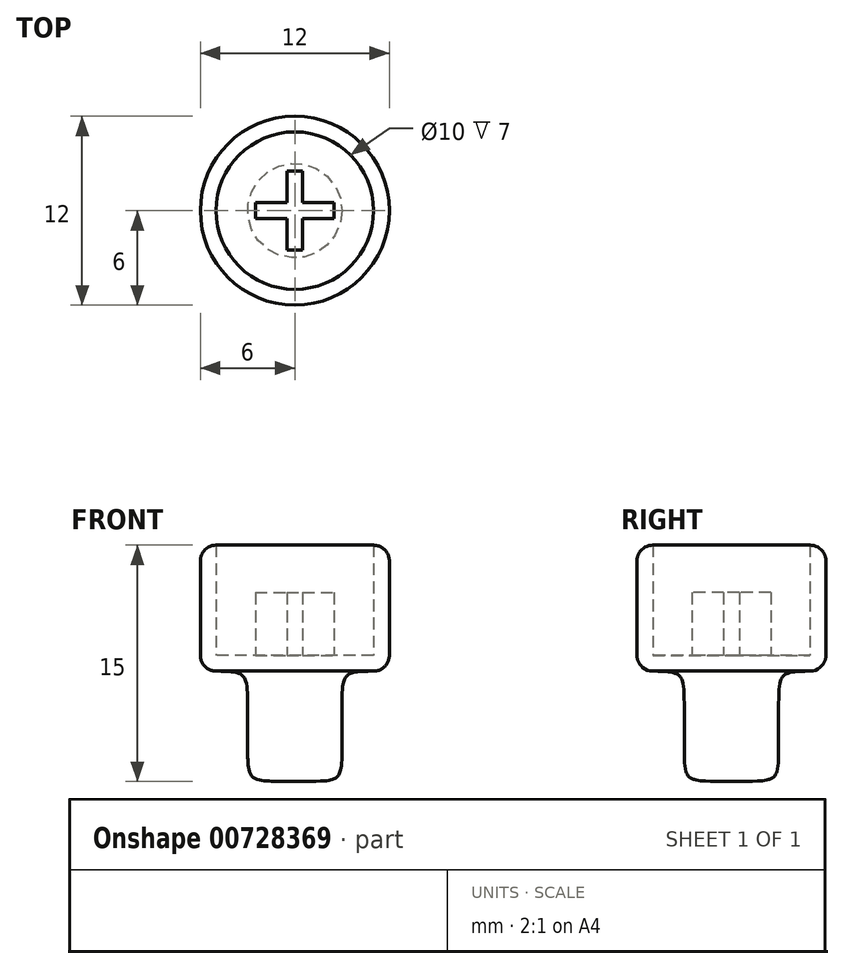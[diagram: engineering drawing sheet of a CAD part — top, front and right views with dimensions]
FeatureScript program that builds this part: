
annotation { "Feature Type Name" : "Feature", "Feature Type Description" : "" }
export const myFeature = defineFeature(function(context is Context, id is Id, definition is map)
    precondition{}
    {
        {
            var Q0;
            Q0=qCreatedBy(makeId("Top.planeOp"),FACE);
            var sketch = newSketch(context, id + "F0", { "sketchPlane" : qUnion([Q0])});
            skCircle(sketch, "E0", {"center": v(0, 0) * mm, "radius": 3 * mm});
            skSolve(sketch);
        }
        {
            var Q0;
            Q0=makeQuery(id+"F0.imprint","IMPRINT",FACE,{"disambiguationData":[TD([[makeQuery(id+"F0.imprint","IMPRINT",EDGE,{"derivedFrom":sQuery(id+"F0.wireOp",EDGE,"E0")}),1.0]])]});
            extrude(context, id + "F1", {"entities" : qUnion([Q0]), "depth" : 7 * mm, "offsetDistance" : 25 * mm});
        }
        {
            var Q0;
            Q0=makeQuery(id+"F1.opExtrude","CAP_FACE",FACE,{"disambiguationData":[OSD([sQuery(id+"F0.wireOp",EDGE,"E0")])],"isStart":false});
            var sketch = newSketch(context, id + "F2", { "sketchPlane" : qUnion([Q0])});
            skCircle(sketch, "E1", {"center": v(0, 0) * mm, "radius": 6 * mm});
            skSolve(sketch);
        }
        {
            var Q0;
            Q0 = qSketchRegion(id + "F2", true);
            extrude(context, id + "F3", {"entities" : qUnion([Q0]), "operationType" : NewBodyOperationType.ADD, "depth" : 2 * mm, "offsetDistance" : 25 * mm});
        }
        {
            var Q0;
            Q0=makeQuery(id+"F3.opExtrude","CAP_FACE",FACE,{"disambiguationData":[OSD([sQuery(id+"F2.wireOp",EDGE,"E1")])],"isStart":false});
            extrude(context, id + "F4", {"entities" : qUnion([Q0]), "operationType" : NewBodyOperationType.ADD, "depth" : 6 * mm, "offsetDistance" : 25 * mm});
        }
        {
            var Q0;
            Q0=makeQuery(id+"F4.opExtrude","CAP_FACE",FACE,{"disambiguationData":[OSD([sQuery(id+"F2.wireOp",EDGE,"E1")])],"isStart":false});
            shell(context, id + "F5", {"entities" : qUnion([Q0]), "thickness" : 1 * mm});
        }
        {
            var Q0;
            {var subQ0=sQuery(id+"F0.wireOp",EDGE,"E0");Q0=makeQuery(id+"F5.opShell","OFFSET_FACE",FACE,{"disambiguationData":[OSD([subQ0]),TDD([makeQuery(id+"F1.opExtrude","CAP_FACE",FACE,{"disambiguationData":[OSD([subQ0])],"isStart":true})])]});}
            var Q1;
            {var subQ0=sQuery(id+"F2.wireOp",EDGE,"E1");Q1=makeQuery(id+"F5.opShell","OFFSET_FACE",FACE,{"disambiguationData":[OSD([subQ0]),TDD([makeQuery(id+"F3.opExtrude","CAP_FACE",FACE,{"disambiguationData":[OSD([subQ0])],"isStart":true})])]});}
            extrude(context, id + "F6", {"entities" : qUnion([Q0]), "operationType" : NewBodyOperationType.ADD, "endBound" : BoundingType.UP_TO_SURFACE, "depth" : 25 * mm, "endBoundEntityFace" : qUnion([Q1]), "offsetDistance" : 25 * mm});
        }
        {
            var Q0;
            {var subQ0=sQuery(id+"F2.wireOp",EDGE,"E1");Q0=makeQuery(id+"F6.boolean.opBoolean","MERGE",FACE,{"derivedFrom":[makeQuery(id+"F5.opShell","OFFSET_FACE",FACE,{"disambiguationData":[OSD([subQ0]),TDD([makeQuery(id+"F3.opExtrude","CAP_FACE",FACE,{"disambiguationData":[OSD([subQ0])],"isStart":true})])]}),makeQuery(id+"F6.opExtrude","CAP_FACE",FACE,{"disambiguationData":[OSD([subQ0])],"isStart":false})]});}
            var sketch = newSketch(context, id + "F7", { "sketchPlane" : qUnion([Q0])});
            skLineSegment(sketch, "E2.bottom", {"start": v(-0.5, 2.5) * mm, "end": v(0.5, 2.5) * mm});
            skLineSegment(sketch, "E2.top", {"start": v(-0.5, -2.5) * mm, "end": v(0.5, -2.5) * mm});
            skLineSegment(sketch, "E2.left", {"start": v(-0.5, 2.5) * mm, "end": v(-0.5, 0.5) * mm});
            skLineSegment(sketch, "E2.right", {"start": v(0.5, 2.5) * mm, "end": v(0.5, 0.5) * mm});
            skLineSegment(sketch, "E3.bottom", {"start": v(-2.5, 0.5) * mm, "end": v(-0.5, 0.5) * mm});
            skLineSegment(sketch, "E3.top", {"start": v(-2.5, -0.5) * mm, "end": v(-0.5, -0.5) * mm});
            skLineSegment(sketch, "E3.left", {"start": v(-2.5, 0.5) * mm, "end": v(-2.5, -0.5) * mm});
            skLineSegment(sketch, "E3.right", {"start": v(2.5, 0.5) * mm, "end": v(2.5, -0.5) * mm});
            skLineSegment(sketch, "E4.trimOffspring", {"start": v(-0.5, -0.5) * mm, "end": v(-0.5, -2.5) * mm});
            skLineSegment(sketch, "E5.trimOffspring", {"start": v(0.5, -0.5) * mm, "end": v(0.5, -2.5) * mm});
            skLineSegment(sketch, "E6.trimOffspring", {"start": v(0.5, 0.5) * mm, "end": v(2.5, 0.5) * mm});
            skLineSegment(sketch, "E7.trimOffspring", {"start": v(0.5, -0.5) * mm, "end": v(2.5, -0.5) * mm});
            skPoint(sketch, "E8", {"position": v(0, 2.5) * mm});
            skPoint(sketch, "E9", {"position": v(0, -2.5) * mm});
            skPoint(sketch, "E10", {"position": v(2.5, 0) * mm});
            skSolve(sketch);
        }
        {
            var Q0;
            Q0 = qSketchRegion(id + "F7", true);
            extrude(context, id + "F8", {"entities" : qUnion([Q0]), "operationType" : NewBodyOperationType.ADD, "depth" : 4 * mm, "offsetDistance" : 25 * mm});
        }
        {
            var Q0;
            Q0=makeQuery(id+"F1.opExtrude","SWEPT_FACE",FACE,{"disambiguationData":[OSD([sQuery(id+"F0.wireOp",EDGE,"E0")])]});
            fillet(context, id + "F9", {"entities" : qUnion([Q0]), "radius" : 2 * mm, "tangentPropagation" : true, "rho" : 0.7, "crossSection" : FilletCrossSection.CONIC, "allowEdgeOverflow" : false});
        }
        {
            var Q0;
            {var subQ0=sQuery(id+"F2.wireOp",EDGE,"E1");Q0=makeQuery(id+"F4.boolean.opBoolean","MERGE",FACE,{"derivedFrom":[makeQuery(id+"F3.opExtrude","SWEPT_FACE",FACE,{"disambiguationData":[OSD([subQ0])]}),makeQuery(id+"F4.opExtrude","SWEPT_FACE",FACE,{"disambiguationData":[OSD([subQ0])]})]});}
            fillet(context, id + "F10", {"entities" : qUnion([Q0]), "radius" : 1 * mm, "tangentPropagation" : true, "allowEdgeOverflow" : false});
        }
    });
